# Revit family: SE-SU-420_GENERADO
name_source: partatom
category: Equipos especializados
units: mm (PartAtom-declared; Revit-internal decimal feet)

## family parameters
Compartido = No
Corte con vacíos al cargar = No
Cota de conector redondo = Diámetro de uso
Número OmniClass = 23.21.21.47
Punto de cálculo de habitación = No
Se basa en plano de trabajo = No
Siempre vertical = Sí
Tipo de pieza = Normal

## types (7) — shared parameters
Conn Plug = EU (SCHUKO 2P+G)
Cycle = 50 Hz
Depth = 529 mm  [stored 1.73556 ft]
Fabricante = SAMMIC S.L.
Foodservice Equipment Identifier = Sí
Height = 448 mm  [stored 1.46982 ft]
Phase = 1
Revision Code = 1
URL = https://www.sammic.com
URL Cutsheet = http://www.sammic.com
Volts = 230 V
Width = 484 mm  [stored 1.58793 ft]
zero-valued in all types: Elevación por defecto

## per-type parameters (varying)
| type | Comentarios de tipo | FL Amps | Modelo | Specification by Manufacturer | Weight in Pounds |
| Vacuum packing machine SE-416 230/50-60/1 | Tabletop model. 16 m³/h. 420 mm | 4 A | 1140636 | 420 mm sealing bar.

16 m³/h Busch vacuum pump.

Vacuum controlled by sensor. | 112 |
| Vacuum packing machine SE-420 230/50-60/1 | Tabletop model. 20 m³/h. 420 mm | 6 A | 1140638 | 420 mm sealing bar.

20 m³/h Busch vacuum pump.

Vacuum controlled by sensor. | 125 |
| Vacuum packing machine SU-416 230/50-60/1 | Tabletop model. 16 m³/h. 420 mm. | 4 A | 1140760 | 420 mm. sealing bar.
16 m³/h Busch vacuum pump.
Vacuum controlled by sensor. | 112 |
| Vacuum packing machine SU-416P 230/50-60/1 | Tabletop model. 16 m³/h. 420 mm. | 4 A | 1140762 | 420 mm. sealing bar.
16 m³/h Busch vacuum pump.
Vacuum controlled by sensor. | 112 |
| Vacuum packing machine SU-420 230/50-60/1 | Tabletop model. 20 m³/h. 420 mm. | 6 A | 1140772 | 420 mm. sealing bar.
20 m³/h Busch vacuum pump.
Vacuum controlled by sensor. | 125 |
| Vacuum packing machine SU-420P 230/50-60/1 | Tabletop model. 20 m³/h. 420 mm. | 6 A | 1140774 | 420 mm. sealing bar.
20 m³/h Busch vacuum pump.
Vacuum controlled by sensor. | 125 |
| Vacuum packing machine SU-420P+ 230/50-60/1 | Tabletop model. 20 m³/h. 420 mm. | 6 A | 1140776 | 420 mm. sealing bar.
20 m³/h Busch vacuum pump.
Vacuum controlled by sensor. | 125 |

note: column(s) folded — value = type name in every type: Descripción

note: [stored X ft] marks values corroborated as IEEE doubles in the binary element streams (Revit-internal decimal feet)
